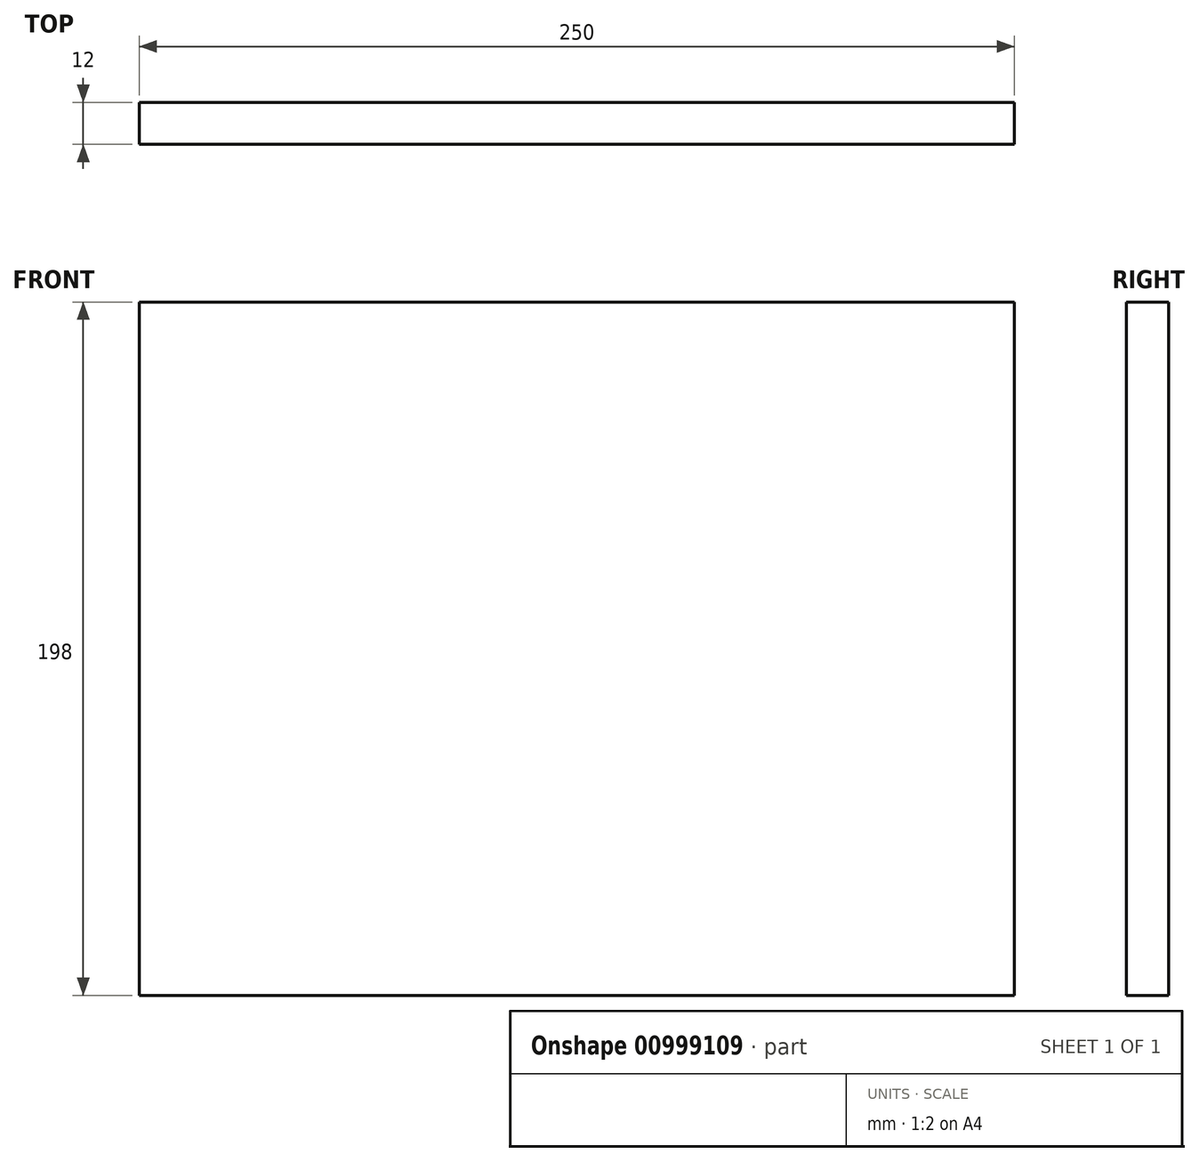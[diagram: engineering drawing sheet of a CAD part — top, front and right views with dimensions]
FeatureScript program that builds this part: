
annotation { "Feature Type Name" : "Feature", "Feature Type Description" : "" }
export const myFeature = defineFeature(function(context is Context, id is Id, definition is map)
    precondition{}
    {
        {
            var Q0;
            Q0=qCreatedBy(makeId("Front.planeOp"),FACE);
            var sketch = newSketch(context, id + "F0", { "sketchPlane" : qUnion([Q0])});
            skLineSegment(sketch, "E0.bottom", {"start": v(-125, 99) * mm, "end": v(125, 99) * mm});
            skLineSegment(sketch, "E0.top", {"start": v(-125, -99) * mm, "end": v(125, -99) * mm});
            skLineSegment(sketch, "E0.left", {"start": v(-125, 99) * mm, "end": v(-125, -99) * mm});
            skLineSegment(sketch, "E0.right", {"start": v(125, 99) * mm, "end": v(125, -99) * mm});
            skPoint(sketch, "E0.middle", {"position": v(0, 0) * mm});
            skSolve(sketch);
        }
        {
            var Q0;
            Q0=makeQuery(id+"F0.imprint","IMPRINT",FACE,{"disambiguationData":[TD([[makeQuery(id+"F0.imprint","IMPRINT",EDGE,{"derivedFrom":sQuery(id+"F0.wireOp",EDGE,"E0.bottom")}),-1.0]])]});
            extrude(context, id + "F1", {"entities" : qUnion([Q0]), "depth" : 12 * mm, "offsetDistance" : 25 * mm});
        }
    });
